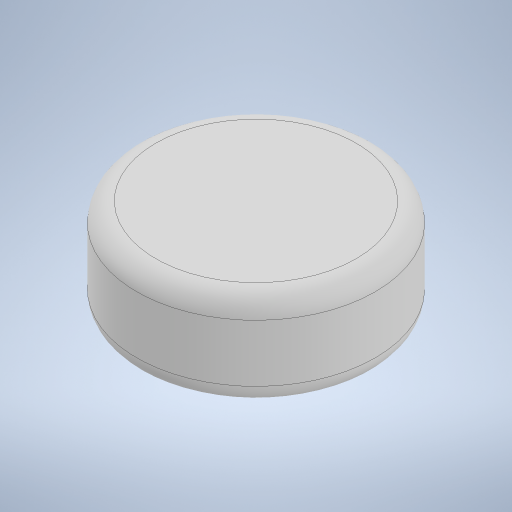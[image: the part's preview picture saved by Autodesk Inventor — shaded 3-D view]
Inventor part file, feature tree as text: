
AUTODESK INVENTOR PART (.ipt)
format: ipt  version: 2023 (Build 270158000, 158)  size: 246,272 bytes
history: native  units: mm
features: sketch x4, extrude x2, fillet x1
ambient origin geometry x8: Origin, YZ Plane, XZ Plane, XY Plane, X Axis, Y Axis, Z Axis, Center Point
bodies: Solid1 (feature_tree)
feature tree (7):
  extrude  "Extrusion1"  Depth=10.0mm TaperAngle=0.0deg
  extrude  "Extrusion2"  Depth=5.0mm TaperAngle=0.0deg
  fillet  "Fillet1"  Radius=2.0mm
  sketch  "Sketch3"  dims[d7=0.872665mm]
  sketch  "Sketch4"
  sketch  "Sketch1"  dims[d0=25.0mm d1=10.0mm d2=0.0mm]
  sketch  "Sketch2"  dims[d3=20.0mm d4=5.0mm d5=0.0mm d6=2.0mm]
